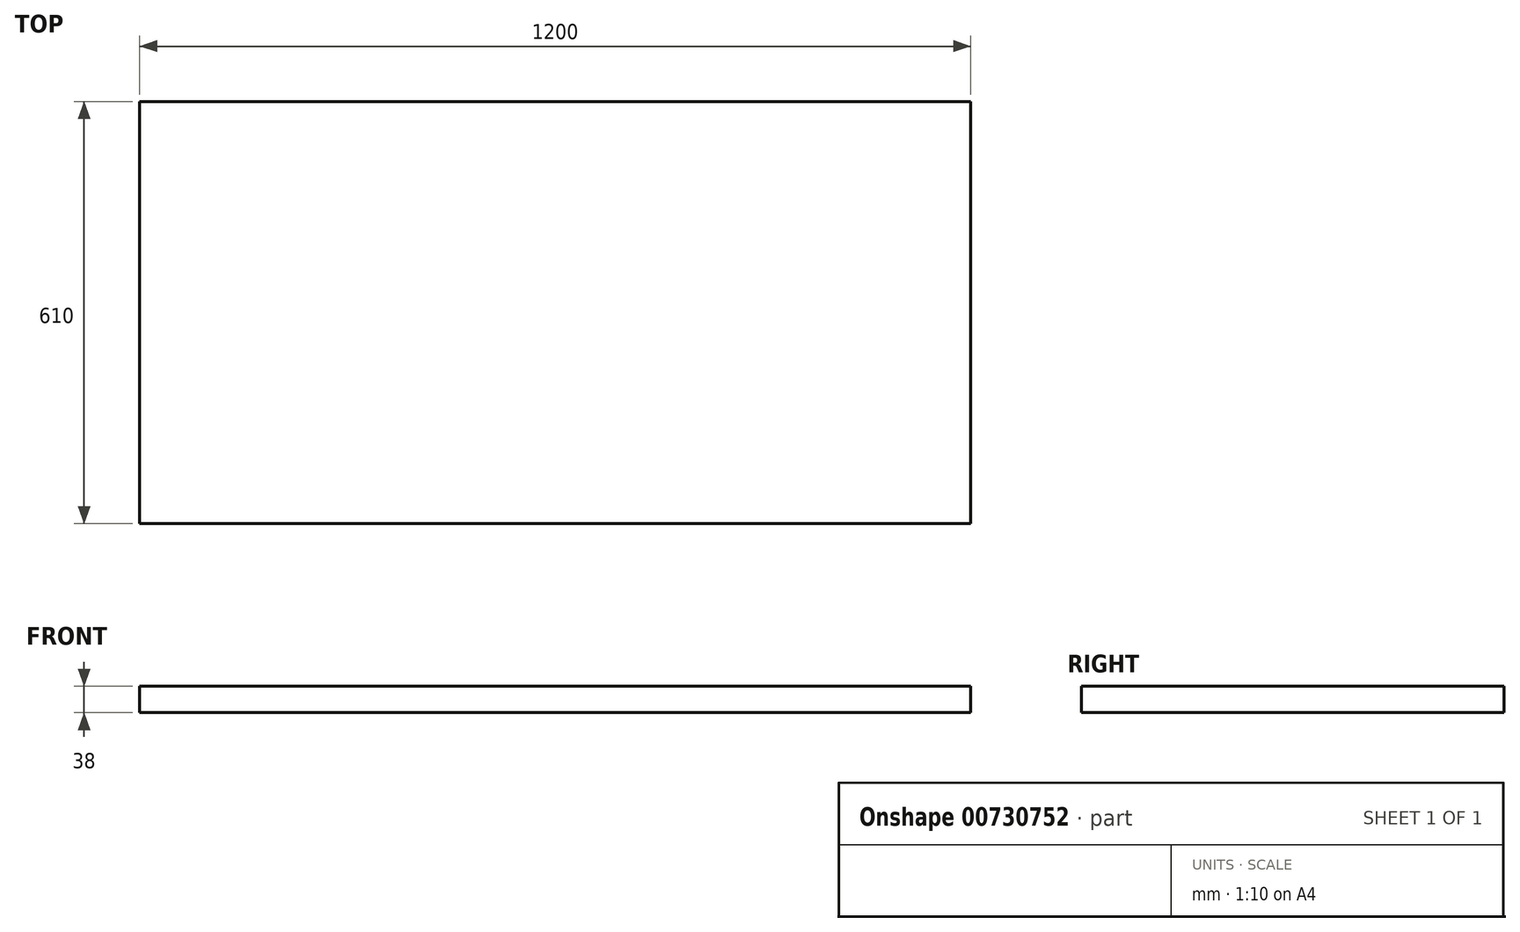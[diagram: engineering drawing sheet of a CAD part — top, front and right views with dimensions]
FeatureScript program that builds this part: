
annotation { "Feature Type Name" : "Feature", "Feature Type Description" : "" }
export const myFeature = defineFeature(function(context is Context, id is Id, definition is map)
    precondition{}
    {
        {
            var Q0;
            Q0=qCreatedBy(makeId("Front.planeOp"),FACE);
            var sketch = newSketch(context, id + "F0", { "sketchPlane" : qUnion([Q0])});
            skLineSegment(sketch, "E0.bottom", {"start": v(600, 19) * mm, "end": v(-600, 19) * mm});
            skLineSegment(sketch, "E0.top", {"start": v(600, -19) * mm, "end": v(-600, -19) * mm});
            skLineSegment(sketch, "E0.left", {"start": v(600, 19) * mm, "end": v(600, -19) * mm});
            skLineSegment(sketch, "E0.right", {"start": v(-600, 19) * mm, "end": v(-600, -19) * mm});
            skPoint(sketch, "E0.middle", {"position": v(0, 0) * mm});
            skSolve(sketch);
        }
        {
            var Q0;
            Q0 = qSketchRegion(id + "F0", true);
            extrude(context, id + "F1", {"entities" : qUnion([Q0]), "endBound" : BoundingType.SYMMETRIC, "depth" : 610 * mm, "offsetDistance" : 25.4 * mm});
        }
    });
